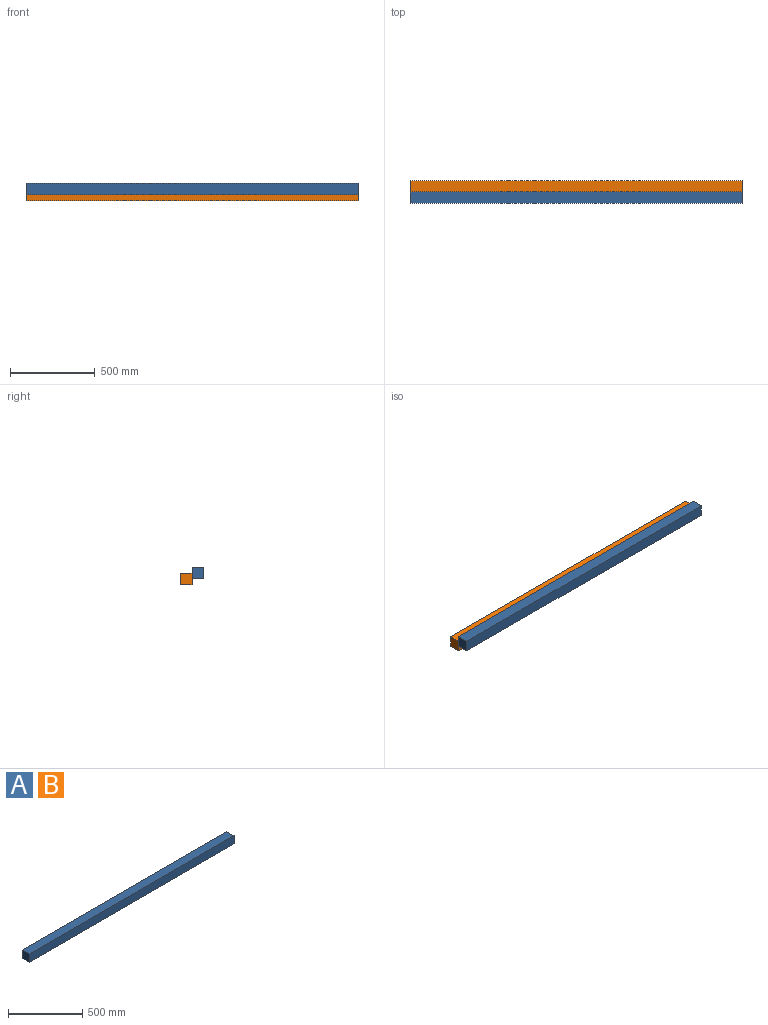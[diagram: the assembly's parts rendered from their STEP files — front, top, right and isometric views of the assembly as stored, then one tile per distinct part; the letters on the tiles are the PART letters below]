
ASSEMBLY  parts=2 mates=1
PART A: 6 faces, bbox 1954.1x67.3x68 mm
  f0: plane 1954.12x67.32mm, normal (0,0,-1), area 131551.4mm2, adj f1,f3,f4,f5
  f1: plane 68.04x67.32mm, normal (1,0,0), area 4580.8mm2, adj f0,f2,f4,f5
  f2: plane 1954.12x67.32mm, normal (0,0,1), area 131551.4mm2, adj f1,f3,f4,f5
  f3: plane 68.04x67.32mm, normal (-1,0,0), area 4580.8mm2, adj f0,f2,f4,f5
  f4: plane 1954.12x68.04mm, normal (0,-1,0), area 132967.1mm2, adj f0,f1,f2,f3
  f5: plane 1954.12x68.04mm, normal (0,1,0), area 132967.1mm2, adj f0,f1,f2,f3
PART B: same geometry as A
PLACE A t=(81.39,-122.52,-254.27)mm
PLACE B t=(81.39,-55.2,-288.29)mm
MATE fastened B.f4 <-> A.f5  axis (0,-1,0) through (-783.24,-123.2,-204.41)mm
